# Revit family: MARK Product_Type_ Dining table_ Family
name_source: partatom
category: Furniture
revit_build: Autodesk Revit 2018 (Build: 20170223_1515(x64)
units: mm (PartAtom-declared; Revit-internal decimal feet)

## family parameters
Always vertical = Yes
Cut with Voids When Loaded = No
OmniClass Number = 23.40.20.00
OmniClass Title = General Furniture and Specialties
Room Calculation Point = No
Shared = No
Work Plane-Based = No

## types (36) — shared parameters
Edge Material = Oak Veneered
Feet Material = Rubber
Manufacturer = MARK Product
Model = Type
Surface Material = Laminate Top
URL = http://www.markproduct.com

## per-type parameters (varying)
| type | FurnitureType |
| Dining Table (1400X600X740X) | Type Range Family : DiningTable 1400X600X740 |
| Dining Table (1600X600X740X) | Type Range Family : DiningTable 1600X600X740 |
| Dining Table (1800X600X740X) | Type Range Family : DiningTable 1800X600X740 |
| Dining Table (2000X600X740X) | Type Range Family : DiningTable 2000X600X740 |
| Dining Table (2200X600X740X) | Type Range Family : DiningTable 2200X600X740 |
| Dining Table (2400X600X740X) | Type Range Family : DiningTable 2400X600X740 |
| Dining Table (2600X600X740X) | Type Range Family : DiningTable 2600X600X740 |
| Dining Table (2800X600X740X) | Type Range Family : DiningTable 2800X600X740 |
| Dining Table (3000X600X740X) | Type Range Family : DiningTable 3000X600X740 |
| Dining Table (1400X800X740X) | Type Range Family : DiningTable 1400X800X740 |
| Dining Table (1600X800X740X) | Type Range Family : DiningTable 1600X800X740 |
| Dining Table (1800X800X740X) | Type Range Family : DiningTable 1800X800X740 |
| Dining Table (2000X800X740X) | Type Range Family : DiningTable 2000X800X740 |
| Dining Table (2200X800X740X) | Type Range Family : DiningTable 2200X800X740 |
| Dining Table (2400X800X740X) | Type Range Family : DiningTable 2400X800X740 |
| Dining Table (2600X800X740X) | Type Range Family : DiningTable 2600X800X740 |
| Dining Table (2800X800X740X) | Type Range Family : DiningTable 2800X800X740 |
| Dining Table (3000X800X740X) | Type Range Family : DiningTable 3000X800X740 |
| Dining Table (1400X1000X740X) | Type Range Family : DiningTable 1400X1000X740 |
| Dining Table (1600X1000X740X) | Type Range Family : DiningTable 1600X1000X740 |
| Dining Table (1800X1000X740X) | Type Range Family : DiningTable 1800X1000X740 |
| Dining Table (2000X1000X740X) | Type Range Family : DiningTable 2000X1000X740 |
| Dining Table (2200X1000X740X) | Type Range Family : DiningTable 2200X1000X740 |
| Dining Table (2400X1000X740X) | Type Range Family : DiningTable 2400X1000X740 |
| Dining Table (2600X1000X740X) | Type Range Family : DiningTable 2600X1000X740 |
| Dining Table (2800X1000X740X) | Type Range Family : DiningTable 2800X1000X740 |
| Dining Table ( 3000X1000X740X) | Type Range Family : DiningTable 3000X1000X740 |
| Dining Table (1400X1200X740X) | Type Range Family : DiningTable 1400X1200X740 |
| Dining Table (1600X1200X740X) | Type Range Family : DiningTable 1600X1200X740 |
| Dining Table (1800X1200X740X) | Type Range Family : DiningTable 1800X1200X740 |
| Dining Table (2000X1200X740X) | Type Range Family : DiningTable 2000X1200X740 |
| Dining Table (2200X1200X740X) | Type Range Family : DiningTable 2200X1200X740 |
| Dining Table (2400X1200X740X) | Type Range Family : DiningTable 2400X1200X740 |
| Dining Table (2600X1200X740X) | Type Range Family : DiningTable 2600X1200X740 |
| Dining Table (2800X1200X740X) | Type Range Family : DiningTable 2800X1200X740 |
| Dining Table (3000X1200X740X) | Type Range Family : DiningTable 3000X1200X740 |

## geometry (parser evidence)
native form markers: Sweep x8
no freeform markers — native parametric forms only
